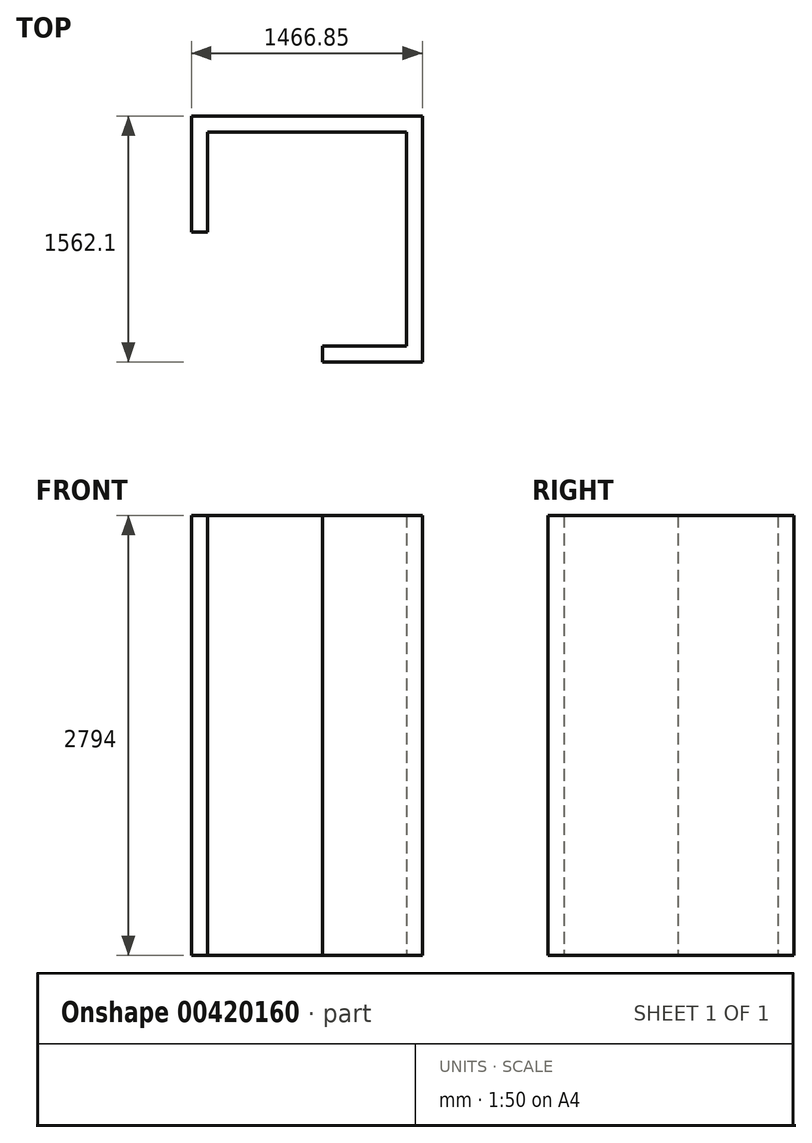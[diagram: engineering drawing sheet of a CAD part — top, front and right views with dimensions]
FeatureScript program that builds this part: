
annotation { "Feature Type Name" : "Feature", "Feature Type Description" : "" }
export const myFeature = defineFeature(function(context is Context, id is Id, definition is map)
    precondition{}
    {
        {
            var Q0;
            Q0=qCreatedBy(makeId("Top.planeOp"),FACE);
            var sketch = newSketch(context, id + "F0", { "sketchPlane" : qUnion([Q0])});
            skLineSegment(sketch, "E0", {"start": v(0, 0) * mm, "end": v(-1263.65, 0) * mm});
            skLineSegment(sketch, "E1", {"start": v(-1263.65, 0) * mm, "end": v(-1263.65, -635) * mm});
            skLineSegment(sketch, "E2", {"start": v(-1263.65, -635) * mm, "end": v(-533.4, -1358.9) * mm});
            skLineSegment(sketch, "E3", {"start": v(-533.4, -1358.9) * mm, "end": v(0, -1358.9) * mm});
            skLineSegment(sketch, "E4", {"start": v(0, -1358.9) * mm, "end": v(0, 0) * mm});
            skSolve(sketch);
        }
        {
            var Q0;
            Q0=qCreatedBy(makeId("Top.planeOp"),FACE);
            var sketch = newSketch(context, id + "F1", { "sketchPlane" : qUnion([Q0])});
            skLineSegment(sketch, "E5", {"start": v(0, 0) * mm, "end": v(-1263.65, 0) * mm});
            skLineSegment(sketch, "E6", {"start": v(-1263.65, 0) * mm, "end": v(-1263.65, -635) * mm});
            skLineSegment(sketch, "E7", {"start": v(0, 0) * mm, "end": v(0, -1358.9) * mm});
            skLineSegment(sketch, "E8", {"start": v(0, -1358.9) * mm, "end": v(-533.4, -1358.9) * mm});
            skLineSegment(sketch, "E9.0", {"start": v(-1365.25, 101.6) * mm, "end": v(-1365.25, -635) * mm});
            skLineSegment(sketch, "E9.1", {"start": v(101.6, 101.6) * mm, "end": v(-1365.25, 101.6) * mm});
            skLineSegment(sketch, "E9.2", {"start": v(101.6, 101.6) * mm, "end": v(101.6, -1460.5) * mm});
            skLineSegment(sketch, "E9.3", {"start": v(101.6, -1460.5) * mm, "end": v(-533.4, -1460.5) * mm});
            skLineSegment(sketch, "E10", {"start": v(-1365.25, -635) * mm, "end": v(-1263.65, -635) * mm});
            skLineSegment(sketch, "E11", {"start": v(-533.4, -1460.5) * mm, "end": v(-533.4, -1358.9) * mm});
            skSolve(sketch);
        }
        {
            var Q0;
            Q0=makeQuery(id+"F1.imprint","IMPRINT",FACE,{"disambiguationData":[TD([[makeQuery(id+"F1.imprint","IMPRINT",EDGE,{"derivedFrom":sQuery(id+"F1.wireOp",EDGE,"E5")}),-1.0]])]});
            extrude(context, id + "F2", {"entities" : qUnion([Q0]), "depth" : 2794 * mm});
        }
    });
